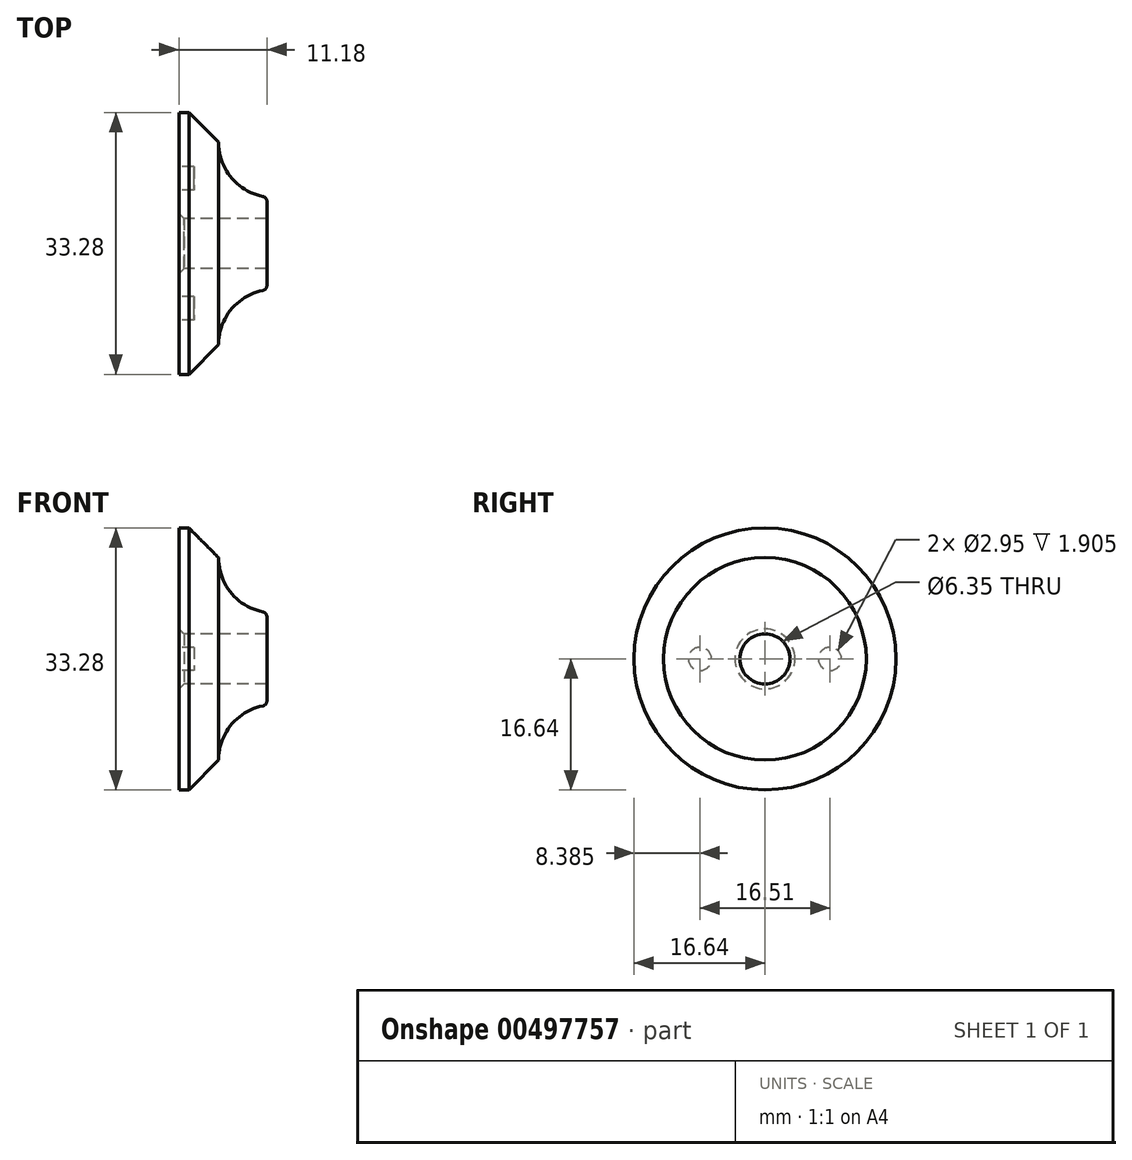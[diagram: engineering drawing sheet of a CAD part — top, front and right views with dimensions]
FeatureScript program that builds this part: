
annotation { "Feature Type Name" : "Feature", "Feature Type Description" : "" }
export const myFeature = defineFeature(function(context is Context, id is Id, definition is map)
    precondition{}
    {
        {
            var Q0;
            Q0=qCreatedBy(makeId("Front.planeOp"),FACE);
            var sketch = newSketch(context, id + "F0", { "sketchPlane" : qUnion([Q0])});
            skLineSegment(sketch, "E0", {"start": v(-1.27, 0) * mm, "end": v(-1.27, 16.64) * mm});
            skLineSegment(sketch, "E1", {"start": v(-1.27, 16.64) * mm, "end": v(0, 16.64) * mm});
            skLineSegment(sketch, "E2", {"start": v(0, 16.64) * mm, "end": v(3.77, 12.87) * mm});
            skLineSegment(sketch, "E3", {"start": v(-1.27, 0) * mm, "end": v(9.9, 0) * mm});
            skLineSegment(sketch, "E4", {"start": v(9.9, 0) * mm, "end": v(9.9, 5.35) * mm});
            skArc(sketch, "E5", {"start": v(3.77, 12.87) * mm, "mid": v(5.34, 8.4) * mm, "end": v(9.4, 5.97) * mm});
            skPoint(sketch, "E6.visualSharp", {"position": v(9.9, 5.9) * mm});
            skArc(sketch, "E6.filletArc", {"start": v(9.9, 5.35) * mm, "mid": v(9.76, 5.75) * mm, "end": v(9.4, 5.97) * mm});
            skSolve(sketch);
        }
        {
            var Q0;
            Q0=makeQuery(id+"F0.imprint","IMPRINT",FACE,{"disambiguationData":[TD([[makeQuery(id+"F0.imprint","IMPRINT",EDGE,{"derivedFrom":sQuery(id+"F0.wireOp",EDGE,"E0")}),-1.0]])]});
            var Q1;
            Q1=sQuery(id+"F0.wireOp",EDGE,"E3");
            revolve(context, id + "F1", {"entities" : qUnion([Q0]), "axis" : qUnion([Q1]), "revolveType" : RevolveType.FULL});
        }
        {
            var Q0;
            Q0=makeQuery(id+"F1.opRevolve","SWEPT_FACE",FACE,{"disambiguationData":[OSD([sQuery(id+"F0.wireOp",EDGE,"E4")])]});
            var sketch = newSketch(context, id + "F2", { "sketchPlane" : qUnion([Q0])});
            skCircle(sketch, "E7", {"center": v(0, 0) * mm, "radius": 3.17 * mm});
            skSolve(sketch);
        }
        {
            var Q0;
            Q0=makeQuery(id+"F1.opRevolve","SWEPT_FACE",FACE,{"disambiguationData":[OSD([sQuery(id+"F0.wireOp",EDGE,"E0")])]});
            var sketch = newSketch(context, id + "F3", { "sketchPlane" : qUnion([Q0])});
            skCircle(sketch, "E8", {"center": v(0, 0) * mm, "radius": 3.18 * mm});
            skSolve(sketch);
        }
        {
            var Q0;
            Q0=makeQuery(id+"F3.imprint","IMPRINT",FACE,{"disambiguationData":[TD([[makeQuery(id+"F3.imprint","IMPRINT",EDGE,{"derivedFrom":sQuery(id+"F3.wireOp",EDGE,"E8")}),1.0]])]});
            extrude(context, id + "F4", {"entities" : qUnion([Q0]), "operationType" : NewBodyOperationType.REMOVE, "oppositeDirection" : true, "depth" : 25.4 * mm});
        }
        {
            var Q0;
            Q0=makeQuery(id+"F3.imprint","IMPRINT",FACE,{"disambiguationData":[TD([[makeQuery(id+"F3.imprint","IMPRINT",EDGE,{"derivedFrom":sQuery(id+"F3.wireOp",EDGE,"E8")}),-1.0]])]});
            var sketch = newSketch(context, id + "F5", { "sketchPlane" : qUnion([Q0])});
            skCircle(sketch, "E9", {"center": v(0, 0) * mm, "radius": 3.81 * mm});
            skSolve(sketch);
        }
        {
            var Q0;
            Q0 = qSketchRegion(id + "F5", true);
            extrude(context, id + "F6", {"entities" : qUnion([Q0]), "operationType" : NewBodyOperationType.REMOVE, "oppositeDirection" : true, "depth" : 25.4 * mm, "hasDraft" : true, "draftAngle" : 45 * degree, "draftPullDirection" : true});
        }
        {
            var Q0;
            Q0=makeQuery(id+"F3.imprint","IMPRINT",FACE,{"disambiguationData":[TD([[makeQuery(id+"F3.imprint","IMPRINT",EDGE,{"derivedFrom":sQuery(id+"F3.wireOp",EDGE,"E8")}),-1.0]])]});
            var sketch = newSketch(context, id + "F7", { "sketchPlane" : qUnion([Q0])});
            skPoint(sketch, "E10.0", {"position": v(0, 0) * mm});
            skCircle(sketch, "E11", {"center": v(-8.26, 0) * mm, "radius": 1.47 * mm});
            skCircle(sketch, "E12.MirrorC", {"center": v(8.26, 0) * mm, "radius": 1.47 * mm});
            skSolve(sketch);
        }
        {
            var Q0;
            Q0 = qSketchRegion(id + "F7", true);
            var Q1;
            Q1=sQuery(id+"F7.wireOp",EDGE,"E11");
            var Q2;
            Q2=sQuery(id+"F7.wireOp",EDGE,"E12.MirrorC");
            extrude(context, id + "F8", {"entities" : qUnion([Q0]), "operationType" : NewBodyOperationType.REMOVE, "surfaceEntities" : qUnion([Q1, Q2]), "oppositeDirection" : true, "depth" : 1.9 * mm});
        }
    });
